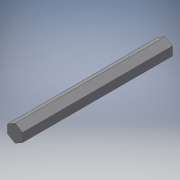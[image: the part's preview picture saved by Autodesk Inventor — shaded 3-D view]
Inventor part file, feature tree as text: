
AUTODESK INVENTOR PART (.ipt)
format: ipt  version: 2018 (Build 220112000, 112)  size: 95,744 bytes
history: native  units: in
note: dims shown in document units (in); Inventor stores cm internally (conversion verified against a paired STEP export)
features: extrude x1, sketch x1
ambient origin geometry x8: Origin, YZ Plane, XZ Plane, XY Plane, X Axis, Y Axis, Z Axis, Center Point
bodies: Solid1 (feature_tree)
feature tree (2):
  extrude  "Extrusion1"  Depth=5.0in TaperAngle=0.0deg
  sketch  "Sketch1"  dims[d0=0.25in d1=5.0in d2=0.0in]
